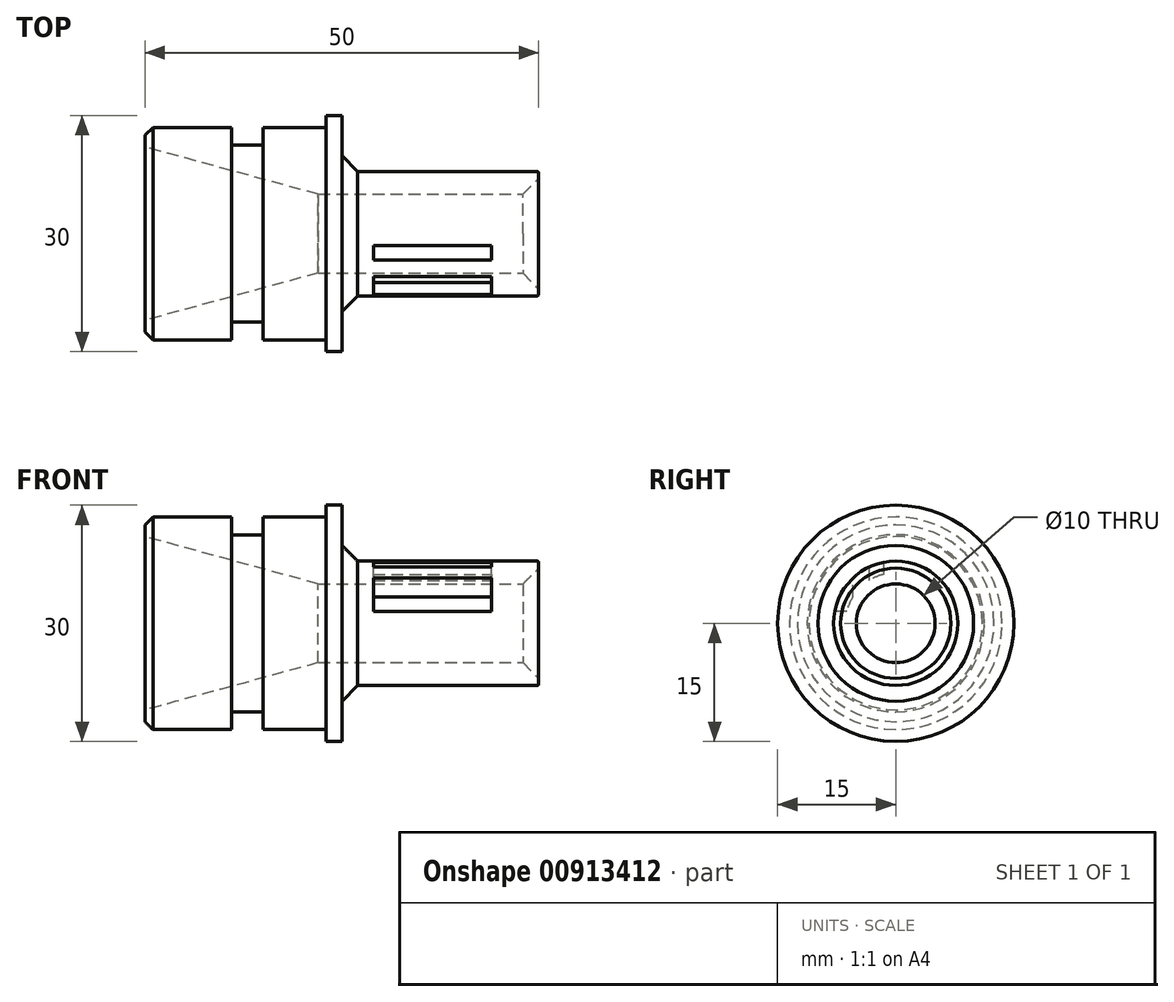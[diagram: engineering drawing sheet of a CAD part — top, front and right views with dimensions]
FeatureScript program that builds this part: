
annotation { "Feature Type Name" : "Feature", "Feature Type Description" : "" }
export const myFeature = defineFeature(function(context is Context, id is Id, definition is map)
    precondition{}
    {
        {
            var Q0;
            Q0=qCreatedBy(makeId("Front.planeOp"),FACE);
            var sketch = newSketch(context, id + "F0", { "sketchPlane" : qUnion([Q0])});
            skLineSegment(sketch, "E0", {"start": v(47.48, 0) * mm, "end": v(-10.61, 0) * mm, "construction": true});
            skLineSegment(sketch, "E1", {"start": v(0, 11) * mm, "end": v(0, 13.5) * mm});
            skLineSegment(sketch, "E2", {"start": v(0, 13.5) * mm, "end": v(11, 13.5) * mm});
            skLineSegment(sketch, "E3", {"start": v(11, 13.5) * mm, "end": v(11, 11.25) * mm});
            skLineSegment(sketch, "E4", {"start": v(11, 11.25) * mm, "end": v(15, 11.25) * mm});
            skLineSegment(sketch, "E5", {"start": v(15, 11.25) * mm, "end": v(15, 13.5) * mm});
            skLineSegment(sketch, "E6", {"start": v(15, 13.5) * mm, "end": v(23, 13.5) * mm});
            skLineSegment(sketch, "E7", {"start": v(23, 13.5) * mm, "end": v(23, 15) * mm});
            skLineSegment(sketch, "E8", {"start": v(23, 15) * mm, "end": v(25, 15) * mm});
            skLineSegment(sketch, "E9", {"start": v(25, 15) * mm, "end": v(25, 7.9) * mm});
            skLineSegment(sketch, "E10", {"start": v(50, 7.9) * mm, "end": v(50, 5) * mm});
            skLineSegment(sketch, "E11", {"start": v(50, 5) * mm, "end": v(22, 5) * mm});
            skLineSegment(sketch, "E12", {"start": v(22, 5) * mm, "end": v(0, 11) * mm});
            skLineSegment(sketch, "E13", {"start": v(50, 7.9) * mm, "end": v(25, 7.9) * mm});
            skSolve(sketch);
        }
        {
            var Q0;
            Q0=makeQuery(id+"F0.imprint","IMPRINT",FACE,{"disambiguationData":[TD([[makeQuery(id+"F0.imprint","IMPRINT",EDGE,{"derivedFrom":sQuery(id+"F0.wireOp",EDGE,"E1")}),-1.0]])]});
            var Q1;
            Q1=sQuery(id+"F0.wireOp",EDGE,"E0");
            revolve(context, id + "F1", {"surfaceOperationType" : NewSurfaceOperationType.NEW, "entities" : qUnion([Q0]), "axis" : qUnion([Q1]), "revolveType" : RevolveType.FULL});
        }
        {
            var Q0;
            Q0=makeQuery(id+"F1.opRevolve","SWEPT_EDGE",EDGE,{"disambiguationData":[OSD([sQuery(id+"F0.wireOp",EDGE,"E10"),sQuery(id+"F0.wireOp",EDGE,"E13")])]});
            fillet(context, id + "F2", {"entities" : qUnion([Q0]), "radius" : 0.2 * mm, "tangentPropagation" : true, "allowEdgeOverflow" : false});
        }
        {
            var Q0;
            Q0=makeQuery(id+"F1.opRevolve","SWEPT_EDGE",EDGE,{"disambiguationData":[OSD([sQuery(id+"F0.wireOp",EDGE,"E10"),sQuery(id+"F0.wireOp",EDGE,"E11")])]});
            var Q1;
            Q1=makeQuery(id+"F1.opRevolve","SWEPT_EDGE",EDGE,{"disambiguationData":[OSD([sQuery(id+"F0.wireOp",EDGE,"E9"),sQuery(id+"F0.wireOp",EDGE,"E13")])]});
            chamfer(context, id + "F3", {"entities" : qUnion([Q0, Q1]), "width" : 2 * mm, "tangentPropagation" : true});
        }
        {
            var Q0;
            Q0=makeQuery(id+"F1.opRevolve","SWEPT_EDGE",EDGE,{"disambiguationData":[OSD([sQuery(id+"F0.wireOp",EDGE,"E1"),sQuery(id+"F0.wireOp",EDGE,"E2")])]});
            chamfer(context, id + "F4", {"entities" : qUnion([Q0]), "width" : 1 * mm, "tangentPropagation" : true});
        }
        {
            var Q0;
            Q0=makeQuery(id+"F1.opRevolve","SWEPT_FACE",FACE,{"disambiguationData":[OSD([sQuery(id+"F0.wireOp",EDGE,"E10")])]});
            cPlane(context, id + "F5", {"entities" : qUnion([Q0]), "cplaneType" : CPlaneType.OFFSET, "offset" : 6 * mm, "oppositeDirection" : true, "width" : 150 * mm, "height" : 150 * mm});
        }
        {
            var Q0;
            Q0=qCreatedBy(id+"F5.planeOp",FACE);
            var sketch = newSketch(context, id + "F6", { "sketchPlane" : qUnion([Q0])});
            skArc(sketch, "E14", {"start": v(-1.5, 6.22) * mm, "mid": v(-2.47, 5.9) * mm, "end": v(-3.37, 5.44) * mm});
            skArc(sketch, "E15", {"start": v(-1.5, 7.76) * mm, "mid": v(-2.45, 7.5) * mm, "end": v(-3.37, 7.15) * mm});
            skLineSegment(sketch, "E16", {"start": v(0, 0) * mm, "end": v(0, 10.56) * mm, "construction": true});
            skLineSegment(sketch, "E17", {"start": v(0, 0) * mm, "end": v(-10.02, 0) * mm, "construction": true});
            skLineSegment(sketch, "E18.0", {"start": v(-3.37, 5.44) * mm, "end": v(-3.37, 7.15) * mm});
            skLineSegment(sketch, "E19.trimOffspring", {"start": v(-1.5, 6.22) * mm, "end": v(-1.5, 7.76) * mm});
            skArc(sketch, "E20.trimOffspring", {"start": v(-5.44, 5.73) * mm, "mid": v(-6.93, 3.8) * mm, "end": v(-7.76, 1.5) * mm});
            skArc(sketch, "E21.trimOffspring", {"start": v(-5.44, 3.37) * mm, "mid": v(-5.9, 2.47) * mm, "end": v(-6.22, 1.5) * mm});
            skLineSegment(sketch, "E22.trimOffspring", {"start": v(-5.44, 3.37) * mm, "end": v(-5.44, 5.73) * mm});
            skLineSegment(sketch, "E23.trimOffspring", {"start": v(-6.22, 1.5) * mm, "end": v(-7.76, 1.5) * mm});
            skSolve(sketch);
        }
        {
            var Q0;
            Q0=makeQuery(id+"F6.imprint","IMPRINT",FACE,{"disambiguationData":[TD([[makeQuery(id+"F6.imprint","IMPRINT",EDGE,{"derivedFrom":sQuery(id+"F6.wireOp",EDGE,"E14")}),-1.0]])]});
            var Q1;
            Q1=makeQuery(id+"F6.imprint","IMPRINT",FACE,{"disambiguationData":[TD([[makeQuery(id+"F6.imprint","IMPRINT",EDGE,{"derivedFrom":sQuery(id+"F6.wireOp",EDGE,"E20.trimOffspring")}),1.0]])]});
            extrude(context, id + "F7", {"entities" : qUnion([Q0, Q1]), "operationType" : NewBodyOperationType.REMOVE, "oppositeDirection" : true, "depth" : 15 * mm, "offsetDistance" : 25 * mm});
        }
    });
